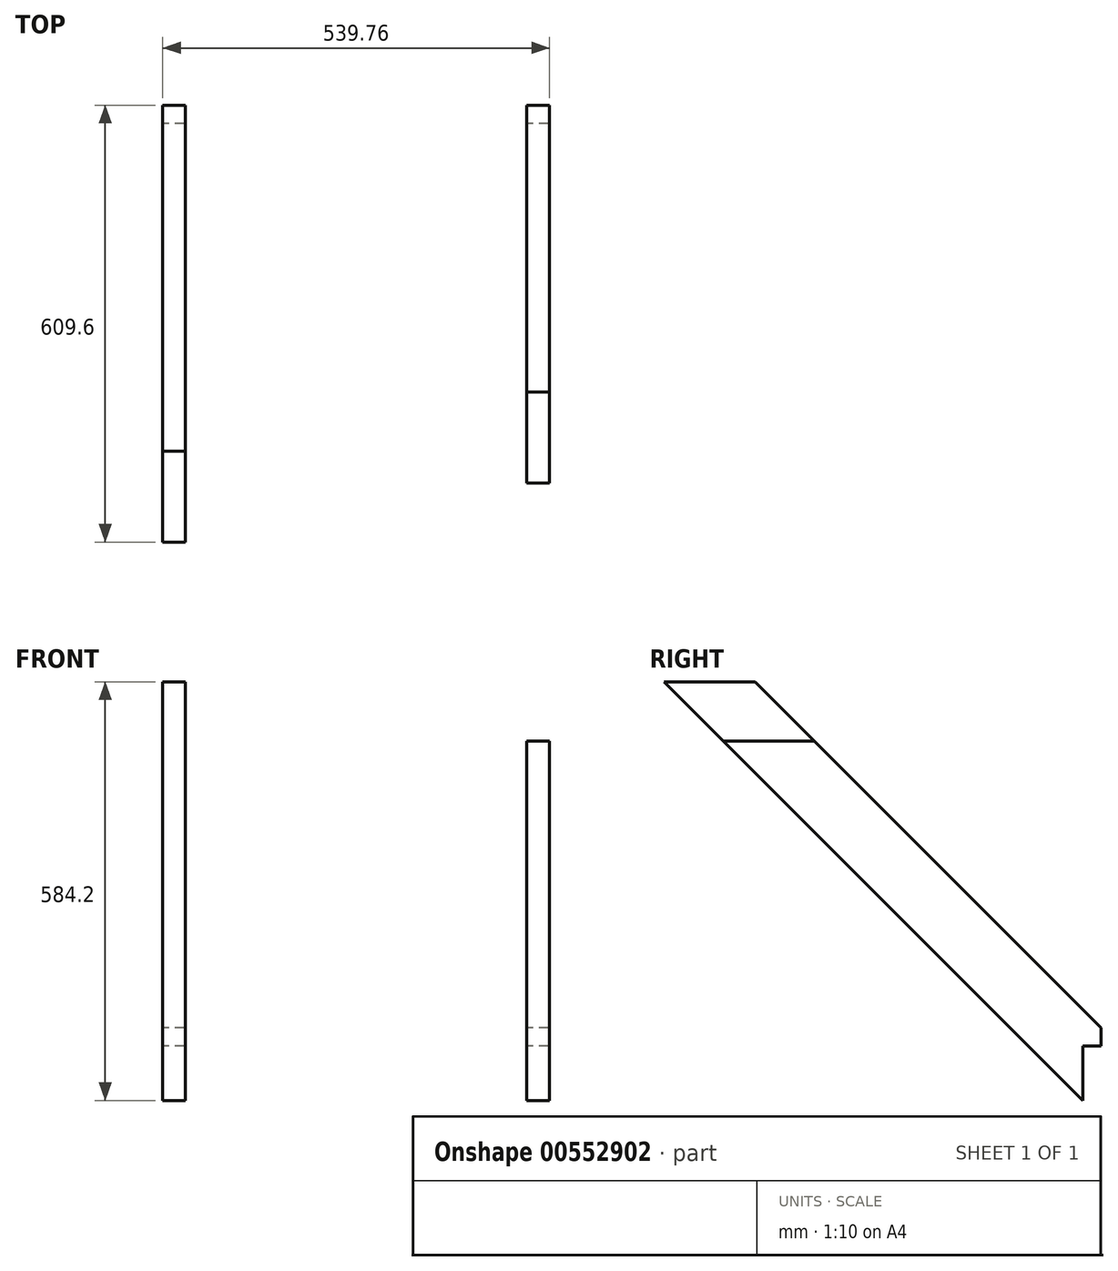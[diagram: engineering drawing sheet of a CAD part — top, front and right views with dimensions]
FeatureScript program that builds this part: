
annotation { "Feature Type Name" : "Feature", "Feature Type Description" : "" }
export const myFeature = defineFeature(function(context is Context, id is Id, definition is map)
    precondition{}
    {
        {
            var Q0;
            Q0=qCreatedBy(makeId("Right.planeOp"),FACE);
            var sketch = newSketch(context, id + "F0", { "sketchPlane" : qUnion([Q0])});
            skLineSegment(sketch, "E0", {"start": v(0, 0) * mm, "end": v(127, 0) * mm});
            skLineSegment(sketch, "E1", {"start": v(127, 0) * mm, "end": v(609.6, -482.6) * mm});
            skLineSegment(sketch, "E2", {"start": v(609.6, -482.6) * mm, "end": v(609.6, -508) * mm});
            skLineSegment(sketch, "E3", {"start": v(609.6, -508) * mm, "end": v(584.2, -508) * mm});
            skLineSegment(sketch, "E4", {"start": v(584.2, -508) * mm, "end": v(584.2, -584.2) * mm});
            skLineSegment(sketch, "E5", {"start": v(584.2, -584.2) * mm, "end": v(0, 0) * mm});
            skSolve(sketch);
        }
        {
            var Q0;
            Q0 = qSketchRegion(id + "F0", true);
            extrude(context, id + "F1", {"entities" : qUnion([Q0]), "endBound" : BoundingType.SYMMETRIC, "depth" : 31.75 * mm, "offsetDistance" : 25.4 * mm});
        }
        {
            var Q0;
            Q0=makeQuery(id+"F1.opExtrude","SWEPT_BODY",BODY,{"disambiguationData":[OSD([sQuery(id+"F0.wireOp",EDGE,"E0"),sQuery(id+"F0.wireOp",EDGE,"E1"),sQuery(id+"F0.wireOp",EDGE,"E2"),sQuery(id+"F0.wireOp",EDGE,"E3"),sQuery(id+"F0.wireOp",EDGE,"E4"),sQuery(id+"F0.wireOp",EDGE,"E5")])]});
            transform(context, id + "F2", {"entities" : qUnion([Q0]), "transformType" : TransformType.TRANSLATION_3D, "dx" : 508 * mm, "dy" : 0 * mm, "dz" : 0 * mm, "makeCopy" : true});
        }
        {
            var Q0;
            Q0=makeQuery(id+"F2.opPattern","COPY",FACE,{"derivedFrom":makeQuery(id+"F1.opExtrude","CAP_FACE",FACE,{"disambiguationData":[OSD([sQuery(id+"F0.wireOp",EDGE,"E0"),sQuery(id+"F0.wireOp",EDGE,"E1"),sQuery(id+"F0.wireOp",EDGE,"E2"),sQuery(id+"F0.wireOp",EDGE,"E3"),sQuery(id+"F0.wireOp",EDGE,"E4"),sQuery(id+"F0.wireOp",EDGE,"E5")])],"isStart":false}),"instanceName":"1"});
            var sketch = newSketch(context, id + "F3", { "sketchPlane" : qUnion([Q0])});
            skLineSegment(sketch, "E6.bottom", {"start": v(209.55, 0) * mm, "end": v(0, 0) * mm});
            skLineSegment(sketch, "E6.top", {"start": v(209.55, -82.55) * mm, "end": v(0, -82.55) * mm});
            skLineSegment(sketch, "E6.left", {"start": v(209.55, 0) * mm, "end": v(209.55, -82.55) * mm});
            skLineSegment(sketch, "E6.right", {"start": v(0, 0) * mm, "end": v(0, -82.55) * mm});
            skSolve(sketch);
        }
        {
            var Q0;
            Q0 = qSketchRegion(id + "F3", true);
            extrude(context, id + "F4", {"entities" : qUnion([Q0]), "operationType" : NewBodyOperationType.REMOVE, "oppositeDirection" : true, "depth" : 31.75 * mm, "offsetDistance" : 25.4 * mm});
        }
    });
